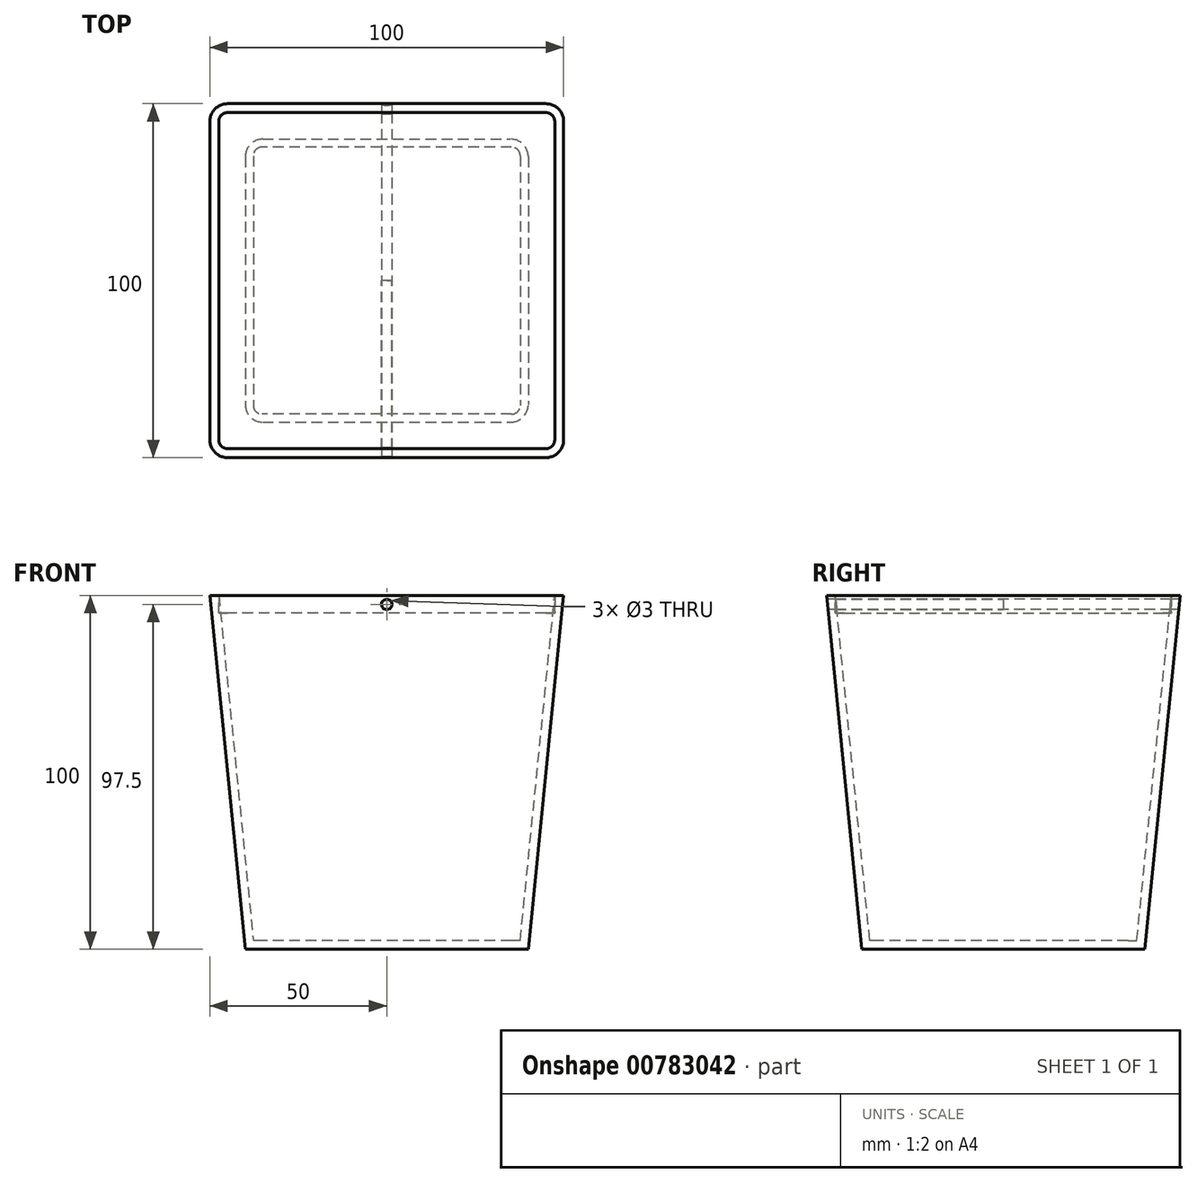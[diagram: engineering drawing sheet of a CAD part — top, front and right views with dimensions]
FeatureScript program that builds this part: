
annotation { "Feature Type Name" : "Feature", "Feature Type Description" : "" }
export const myFeature = defineFeature(function(context is Context, id is Id, definition is map)
    precondition{}
    {
        {
            var Q0;
            Q0=qCreatedBy(makeId("Top.planeOp"),FACE);
            var sketch = newSketch(context, id + "F0", { "sketchPlane" : qUnion([Q0])});
            skLineSegment(sketch, "E0.bottom", {"start": v(50, 50) * mm, "end": v(-50, 50) * mm});
            skLineSegment(sketch, "E0.top", {"start": v(50, -50) * mm, "end": v(-50, -50) * mm});
            skLineSegment(sketch, "E0.left", {"start": v(50, 50) * mm, "end": v(50, -50) * mm});
            skLineSegment(sketch, "E0.right", {"start": v(-50, 50) * mm, "end": v(-50, -50) * mm});
            skPoint(sketch, "E0.middle", {"position": v(0, 0) * mm});
            skSolve(sketch);
        }
        {
            var Q0;
            Q0=qCreatedBy(makeId("Top.planeOp"),FACE);
            cPlane(context, id + "F1", {"entities" : qUnion([Q0]), "cplaneType" : CPlaneType.OFFSET, "offset" : 100 * mm, "oppositeDirection" : true, "width" : 150 * mm, "height" : 150 * mm});
        }
        {
            var Q0;
            Q0=qCreatedBy(id+"F1.planeOp",FACE);
            var sketch = newSketch(context, id + "F2", { "sketchPlane" : qUnion([Q0])});
            skPoint(sketch, "E1.0", {"position": v(0, 0) * mm});
            skLineSegment(sketch, "E2.bottom", {"start": v(-40, 40) * mm, "end": v(40, 40) * mm});
            skLineSegment(sketch, "E2.top", {"start": v(-40, -40) * mm, "end": v(40, -40) * mm});
            skLineSegment(sketch, "E2.left", {"start": v(-40, 40) * mm, "end": v(-40, -40) * mm});
            skLineSegment(sketch, "E2.right", {"start": v(40, 40) * mm, "end": v(40, -40) * mm});
            skSolve(sketch);
        }
        {
            var Q0;
            Q0=makeQuery(id+"F0.imprint","IMPRINT",FACE,{"disambiguationData":[TD([[makeQuery(id+"F0.imprint","IMPRINT",EDGE,{"derivedFrom":sQuery(id+"F0.wireOp",EDGE,"E0.bottom")}),1.0]])]});
            var Q1;
            Q1=makeQuery(id+"F2.imprint","IMPRINT",FACE,{"disambiguationData":[TD([[makeQuery(id+"F2.imprint","IMPRINT",EDGE,{"derivedFrom":sQuery(id+"F2.wireOp",EDGE,"E2.bottom")}),-1.0]])]});
            loft(context, id + "F3", {"sheetProfilesArray" : [{ "sheetProfileEntities" : qUnion([Q0]) }, { "sheetProfileEntities" : qUnion([Q1]) }]});
        }
        {
            var Q0;
            Q0=makeQuery(id+"F3.opLoft","SWEPT_EDGE",EDGE,{"disambiguationData":[OSD([sQuery(id+"F0.wireOp",EDGE,"E0.bottom"),sQuery(id+"F0.wireOp",EDGE,"E0.left"),sQuery(id+"F2.wireOp",EDGE,"E2.bottom"),sQuery(id+"F2.wireOp",EDGE,"E2.right")])]});
            var Q1;
            Q1=makeQuery(id+"F3.opLoft","SWEPT_EDGE",EDGE,{"disambiguationData":[OSD([sQuery(id+"F0.wireOp",EDGE,"E0.bottom"),sQuery(id+"F0.wireOp",EDGE,"E0.right"),sQuery(id+"F2.wireOp",EDGE,"E2.bottom"),sQuery(id+"F2.wireOp",EDGE,"E2.left")])]});
            var Q2;
            Q2=makeQuery(id+"F3.opLoft","SWEPT_EDGE",EDGE,{"disambiguationData":[OSD([sQuery(id+"F0.wireOp",EDGE,"E0.top"),sQuery(id+"F0.wireOp",EDGE,"E0.right"),sQuery(id+"F2.wireOp",EDGE,"E2.top"),sQuery(id+"F2.wireOp",EDGE,"E2.left")])]});
            var Q3;
            Q3=makeQuery(id+"F3.opLoft","SWEPT_EDGE",EDGE,{"disambiguationData":[OSD([sQuery(id+"F0.wireOp",EDGE,"E0.top"),sQuery(id+"F0.wireOp",EDGE,"E0.left"),sQuery(id+"F2.wireOp",EDGE,"E2.top"),sQuery(id+"F2.wireOp",EDGE,"E2.right")])]});
            fillet(context, id + "F4", {"entities" : qUnion([Q0, Q1, Q2, Q3]), "radius" : 5 * mm, "tangentPropagation" : true, "allowEdgeOverflow" : false});
        }
        {
            var Q0;
            Q0=makeQuery(id+"F3.opLoft","CAP_FACE",FACE,{"disambiguationData":[OSD([makeQuery(id+"F0.imprint","IMPRINT",FACE,{"disambiguationData":[TD([[makeQuery(id+"F0.imprint","IMPRINT",EDGE,{"derivedFrom":sQuery(id+"F0.wireOp",EDGE,"E0.bottom")}),1.0]])]})])],"isStart":true});
            shell(context, id + "F5", {"entities" : qUnion([Q0]), "thickness" : 2.5 * mm});
        }
        {
            var Q0;
            Q0=qCreatedBy(makeId("Top.planeOp"),FACE);
            var sketch = newSketch(context, id + "F6", { "sketchPlane" : qUnion([Q0])});
            skLineSegment(sketch, "E3.0", {"start": v(-47.49, -45) * mm, "end": v(-47.49, 45) * mm});
            skEllipticalArc(sketch, "E4.0", {});
            skLineSegment(sketch, "E5.0", {"start": v(-45, 47.49) * mm, "end": v(45, 47.49) * mm});
            skEllipticalArc(sketch, "E6.0", {});
            skLineSegment(sketch, "E7.0", {"start": v(47.49, 45) * mm, "end": v(47.49, -45) * mm});
            skEllipticalArc(sketch, "E8.0", {});
            skLineSegment(sketch, "E9.0", {"start": v(45, -47.49) * mm, "end": v(-45, -47.49) * mm});
            skEllipticalArc(sketch, "E10.0", {});
            const initialGuessF6  = {"E4.0": [-0.04497506218943956, 0.04497506218943955, 0.707106781186547, -0.7071067811865481, 0.002524876234590519, 0.0025, 2.361145066127935, 3.922040241051658], "E6.0": [0.044975062189439544, 0.04497506218943956, 0.7071067811865469, 0.7071067811865482, 0.002524876234590519, 0.0025, 5.502737719717721, 0.7804475874618607], "E8.0": [0.04497506218943956, -0.04497506218943956, -0.707106781186547, 0.7071067811865481, 0.002524876234590519, 0.0025, 2.361145066127935, 3.922040241051658], "E10.0": [-0.044975062189439544, -0.044975062189439564, -0.7071067811865469, -0.7071067811865482, 0.002524876234590519, 0.0025, 5.502737719717721, 0.7804475874618607]};
            skSetInitialGuess(sketch, initialGuessF6);
            skSolve(sketch);
        }
        {
            var Q0;
            Q0 = qSketchRegion(id + "F6", true);
            extrude(context, id + "F7", {"entities" : qUnion([Q0]), "oppositeDirection" : true, "depth" : 5 * mm, "offsetDistance" : 25 * mm});
        }
        {
            var Q0;
            Q0=qCreatedBy(makeId("Front.planeOp"),FACE);
            var sketch = newSketch(context, id + "F8", { "sketchPlane" : qUnion([Q0])});
            skLineSegment(sketch, "E11", {"start": v(0, 0) * mm, "end": v(0, -5) * mm, "construction": true});
            skCircle(sketch, "E12", {"center": v(0, -2.5) * mm, "radius": 1.5 * mm});
            skSolve(sketch);
        }
        {
            var Q0;
            Q0 = qSketchRegion(id + "F8", true);
            extrude(context, id + "F9", {"entities" : qUnion([Q0]), "operationType" : NewBodyOperationType.REMOVE, "endBound" : BoundingType.SYMMETRIC, "oppositeDirection" : true, "depth" : 131.2 * mm, "offsetDistance" : 25 * mm});
        }
        {
            var Q0;
            Q0 = qSketchRegion(id + "F8", true);
            var Q1;
            Q1=makeQuery(id+"F7.opExtrude","SWEPT_FACE",FACE,{"disambiguationData":[OSD([sQuery(id+"F6.wireOp",EDGE,"E9.0")])]});
            extrude(context, id + "F10", {"entities" : qUnion([Q0]), "endBound" : BoundingType.UP_TO_SURFACE, "depth" : 25 * mm, "endBoundEntityFace" : qUnion([Q1]), "offsetDistance" : 25 * mm});
        }
        {
            var Q0;
            Q0 = qSketchRegion(id + "F8", true);
            var Q1;
            Q1=makeQuery(id+"F7.opExtrude","SWEPT_FACE",FACE,{"disambiguationData":[OSD([sQuery(id+"F6.wireOp",EDGE,"E5.0")])]});
            extrude(context, id + "F11", {"entities" : qUnion([Q0]), "endBound" : BoundingType.UP_TO_SURFACE, "oppositeDirection" : true, "depth" : 25 * mm, "endBoundEntityFace" : qUnion([Q1]), "offsetDistance" : 25 * mm});
        }
    });
